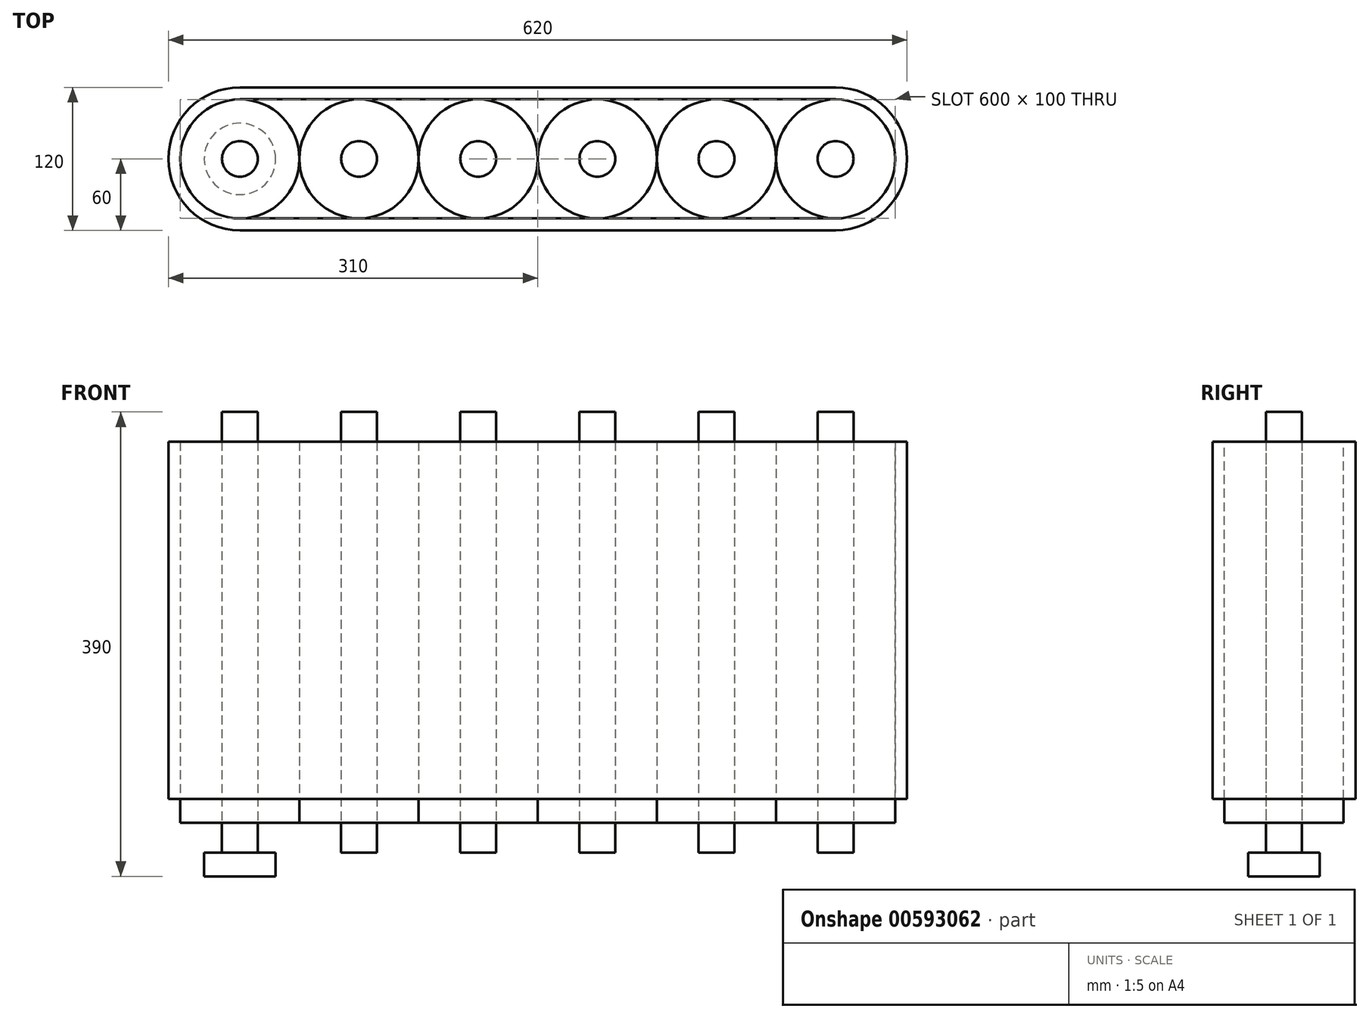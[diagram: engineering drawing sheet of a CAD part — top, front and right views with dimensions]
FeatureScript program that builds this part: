
annotation { "Feature Type Name" : "Feature", "Feature Type Description" : "" }
export const myFeature = defineFeature(function(context is Context, id is Id, definition is map)
    precondition{}
    {
        {
            var Q0;
            Q0=qCreatedBy(makeId("Top.planeOp"),FACE);
            var sketch = newSketch(context, id + "F0", { "sketchPlane" : qUnion([Q0])});
            skCircle(sketch, "E0", {"center": v(0, 0) * mm, "radius": 50 * mm});
            skLineSegment(sketch, "E1", {"start": v(0, 0) * mm, "end": v(100, 0) * mm, "construction": true});
            skCircle(sketch, "E2", {"center": v(100, 0) * mm, "radius": 50 * mm});
            skLineSegment(sketch, "E3", {"start": v(100, 0) * mm, "end": v(200, 0) * mm, "construction": true});
            skLineSegment(sketch, "E4", {"start": v(200, 0) * mm, "end": v(300, 0) * mm, "construction": true});
            skLineSegment(sketch, "E5", {"start": v(300, 0) * mm, "end": v(400, 0) * mm, "construction": true});
            skLineSegment(sketch, "E6", {"start": v(400, 0) * mm, "end": v(500, 0) * mm, "construction": true});
            skCircle(sketch, "E7", {"center": v(200, 0) * mm, "radius": 50 * mm});
            skCircle(sketch, "E8", {"center": v(300, 0) * mm, "radius": 50 * mm});
            skCircle(sketch, "E9", {"center": v(400, 0) * mm, "radius": 50 * mm});
            skCircle(sketch, "E10", {"center": v(500, 0) * mm, "radius": 50 * mm});
            skSolve(sketch);
        }
        {
            var Q0;
            Q0 = qSketchRegion(id + "F0", true);
            extrude(context, id + "F1", {"entities" : qUnion([Q0]), "depth" : 300 * mm, "offsetDistance" : 25 * mm});
        }
        {
            var Q0;
            Q0 = qSketchRegion(id + "F0", true);
            extrude(context, id + "F2", {"entities" : qUnion([Q0]), "oppositeDirection" : true, "depth" : 20 * mm, "offsetDistance" : 25 * mm});
        }
        {
            var Q0;
            Q0=makeQuery(id+"F2.opExtrude","CAP_FACE",FACE,{"disambiguationData":[OSD([sQuery(id+"F0.wireOp",EDGE,"E0")])],"isStart":false});
            var sketch = newSketch(context, id + "F3", { "sketchPlane" : qUnion([Q0])});
            skCircle(sketch, "E11", {"center": v(0, 0) * mm, "radius": 15 * mm});
            skCircle(sketch, "E12", {"center": v(100, 0) * mm, "radius": 15 * mm});
            skCircle(sketch, "E13", {"center": v(200, 0) * mm, "radius": 15 * mm});
            skCircle(sketch, "E14", {"center": v(300, 0) * mm, "radius": 15 * mm});
            skCircle(sketch, "E15", {"center": v(400, 0) * mm, "radius": 15 * mm});
            skCircle(sketch, "E16", {"center": v(500, 0) * mm, "radius": 15 * mm});
            skSolve(sketch);
        }
        {
            var Q0;
            Q0 = qSketchRegion(id + "F3", true);
            extrude(context, id + "F4", {"entities" : qUnion([Q0]), "depth" : 25 * mm, "offsetDistance" : 25 * mm});
        }
        {
            var Q0;
            Q0 = qSketchRegion(id + "F3", true);
            extrude(context, id + "F5", {"entities" : qUnion([Q0]), "oppositeDirection" : true, "depth" : 345 * mm, "offsetDistance" : 25 * mm});
        }
        {
            var Q0;
            Q0=makeQuery(id+"F4.opExtrude","CAP_FACE",FACE,{"disambiguationData":[OSD([sQuery(id+"F3.wireOp",EDGE,"E11")])],"isStart":false});
            var sketch = newSketch(context, id + "F6", { "sketchPlane" : qUnion([Q0])});
            skCircle(sketch, "E17", {"center": v(0, 0) * mm, "radius": 30 * mm});
            skSolve(sketch);
        }
        {
            var Q0;
            Q0 = qSketchRegion(id + "F6", true);
            extrude(context, id + "F7", {"entities" : qUnion([Q0]), "depth" : 20 * mm, "offsetDistance" : 25 * mm});
        }
        {
            var Q0;
            Q0=makeQuery(id+"F1.opExtrude","CAP_FACE",FACE,{"disambiguationData":[OSD([sQuery(id+"F0.wireOp",EDGE,"E0")])],"isStart":false});
            var sketch = newSketch(context, id + "F8", { "sketchPlane" : qUnion([Q0])});
            skArc(sketch, "E18", {"start": v(0, 60) * mm, "mid": v(-60, 0) * mm, "end": v(0, -60) * mm});
            skLineSegment(sketch, "E19", {"start": v(0, 60) * mm, "end": v(500, 60) * mm});
            skLineSegment(sketch, "E20", {"start": v(0, -60) * mm, "end": v(500, -60) * mm});
            skArc(sketch, "E21", {"start": v(500, -60) * mm, "mid": v(560, 0) * mm, "end": v(500, 60) * mm});
            skLineSegment(sketch, "E22.0", {"start": v(0, 50) * mm, "end": v(500, 50) * mm});
            skArc(sketch, "E22.1", {"start": v(0, 50) * mm, "mid": v(-50, 0) * mm, "end": v(0, -50) * mm});
            skLineSegment(sketch, "E22.2", {"start": v(0, -50) * mm, "end": v(500, -50) * mm});
            skArc(sketch, "E22.3", {"start": v(500, -50) * mm, "mid": v(550, 0) * mm, "end": v(500, 50) * mm});
            skSolve(sketch);
        }
        {
            var Q0;
            Q0 = qSketchRegion(id + "F8", true);
            extrude(context, id + "F9", {"entities" : qUnion([Q0]), "oppositeDirection" : true, "depth" : 300 * mm, "offsetDistance" : 25 * mm});
        }
    });
